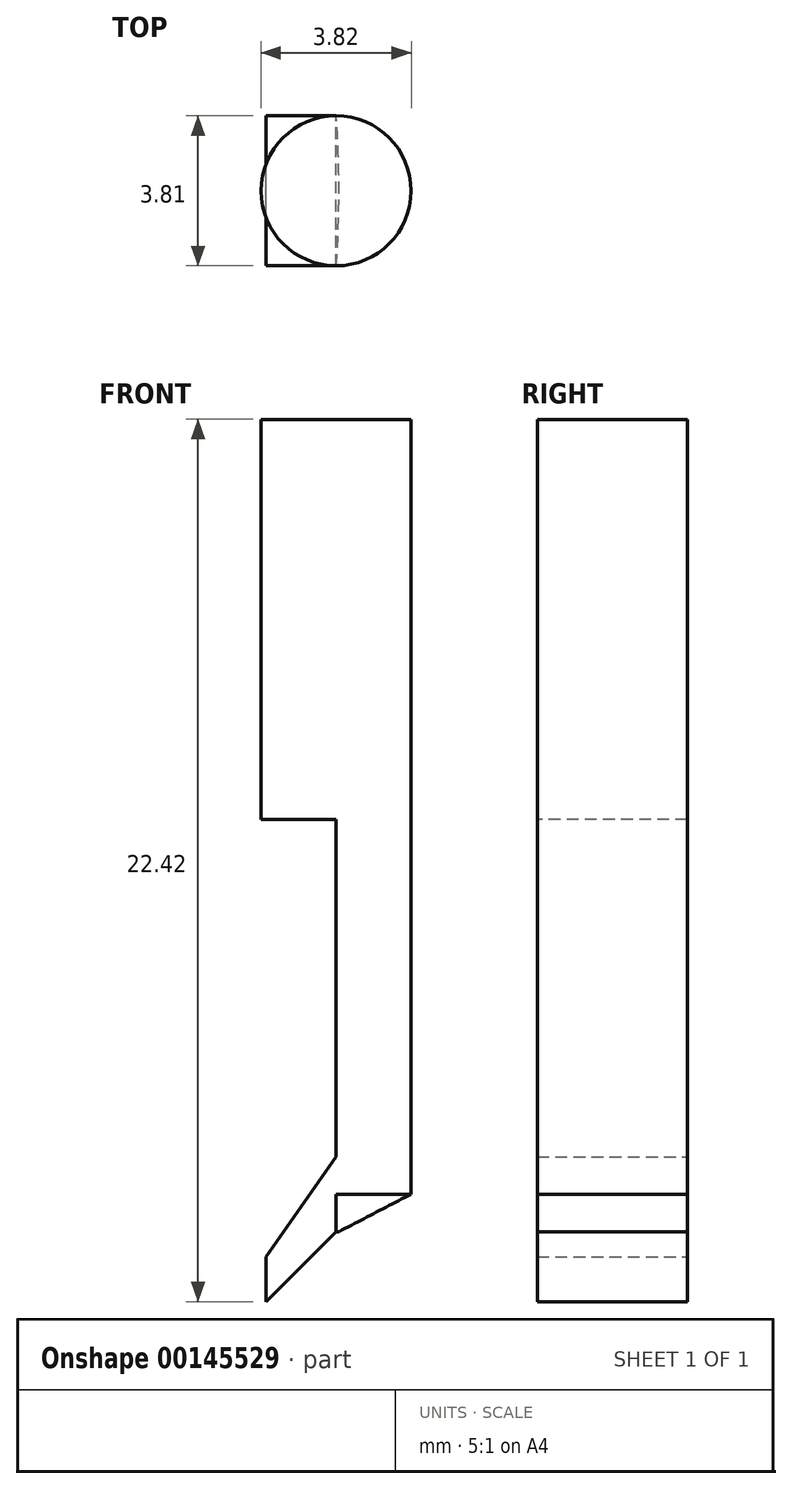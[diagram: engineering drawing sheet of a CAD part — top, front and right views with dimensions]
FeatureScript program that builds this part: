
annotation { "Feature Type Name" : "Feature", "Feature Type Description" : "" }
export const myFeature = defineFeature(function(context is Context, id is Id, definition is map)
    precondition{}
    {
        {
            var Q0;
            Q0=qCreatedBy(makeId("Top.planeOp"),FACE);
            cPlane(context, id + "F0", {"entities" : qUnion([Q0]), "cplaneType" : CPlaneType.OFFSET, "offset" : 0.95 * mm, "width" : 152.4 * mm, "height" : 152.4 * mm});
        }
        {
            var Q0;
            Q0=qCreatedBy(makeId("Front.planeOp"),FACE);
            var sketch = newSketch(context, id + "F1", { "sketchPlane" : qUnion([Q0])});
            skLineSegment(sketch, "E0", {"start": v(0, 0) * mm, "end": v(-1.78, -1.78) * mm});
            skLineSegment(sketch, "E1", {"start": v(-1.78, -1.78) * mm, "end": v(-1.78, -0.63) * mm});
            skLineSegment(sketch, "E2", {"start": v(-1.78, -0.63) * mm, "end": v(0, 1.9) * mm});
            skLineSegment(sketch, "E3", {"start": v(0, 1.9) * mm, "end": v(0, 0) * mm});
            skSolve(sketch);
        }
        {
            var Q0;
            Q0 = qSketchRegion(id + "F1", true);
            extrude(context, id + "F2", {"entities" : qUnion([Q0]), "depth" : 3.8 * mm});
        }
        {
            var Q0;
            Q0=qCreatedBy(id+"F0.planeOp",FACE);
            var sketch = newSketch(context, id + "F3", { "sketchPlane" : qUnion([Q0])});
            skArc(sketch, "E4", {"start": v(0, -3.81) * mm, "mid": v(1.9, -1.9) * mm, "end": v(0, 0) * mm});
            skLineSegment(sketch, "E5", {"start": v(0, 0) * mm, "end": v(0, -3.81) * mm});
            skSolve(sketch);
        }
        {
            var Q0;
            Q0 = qSketchRegion(id + "F3", true);
            extrude(context, id + "F4", {"entities" : qUnion([Q0]), "operationType" : NewBodyOperationType.ADD, "depth" : 9.52 * mm});
        }
        {
            var Q0;
            Q0=makeQuery(id+"F4.opExtrude","CAP_FACE",FACE,{"disambiguationData":[OSD([sQuery(id+"F3.wireOp",EDGE,"E4"),sQuery(id+"F3.wireOp",EDGE,"E5")])],"isStart":false});
            var sketch = newSketch(context, id + "F5", { "sketchPlane" : qUnion([Q0])});
            skCircle(sketch, "E6", {"center": v(0, -1.9) * mm, "radius": 1.9 * mm});
            skSolve(sketch);
        }
        {
            var Q0;
            Q0 = qSketchRegion(id + "F5", true);
            extrude(context, id + "F6", {"entities" : qUnion([Q0]), "operationType" : NewBodyOperationType.ADD, "depth" : 10.16 * mm});
        }
        {
            var Q0;
            Q0=qCreatedBy(makeId("Top.planeOp"),FACE);
            var sketch = newSketch(context, id + "F7", { "sketchPlane" : qUnion([Q0])});
            skArc(sketch, "E7", {"start": v(0, -3.81) * mm, "mid": v(0.07, -1.9) * mm, "end": v(0, 0) * mm});
            skLineSegment(sketch, "E8", {"start": v(0, -3.81) * mm, "end": v(0, 0) * mm});
            skSolve(sketch);
        }
        {
            var Q1;
            Q1=makeQuery(id+"F4.opExtrude","CAP_FACE",FACE,{"disambiguationData":[OSD([sQuery(id+"F3.wireOp",EDGE,"E4"),sQuery(id+"F3.wireOp",EDGE,"E5")])],"isStart":true});
            var Q2;
            Q2=makeQuery(id+"F7.imprint","IMPRINT",FACE,{"disambiguationData":[TD([[makeQuery(id+"F7.imprint","IMPRINT",EDGE,{"derivedFrom":sQuery(id+"F7.wireOp",EDGE,"E7")}),1.0]])]});
            loft(context, id + "F8", {"operationType" : NewBodyOperationType.ADD, "sheetProfilesArray" : [{ "sheetProfileEntities" : qUnion([Q1]) }, { "sheetProfileEntities" : qUnion([Q2]) }]});
        }
    });
